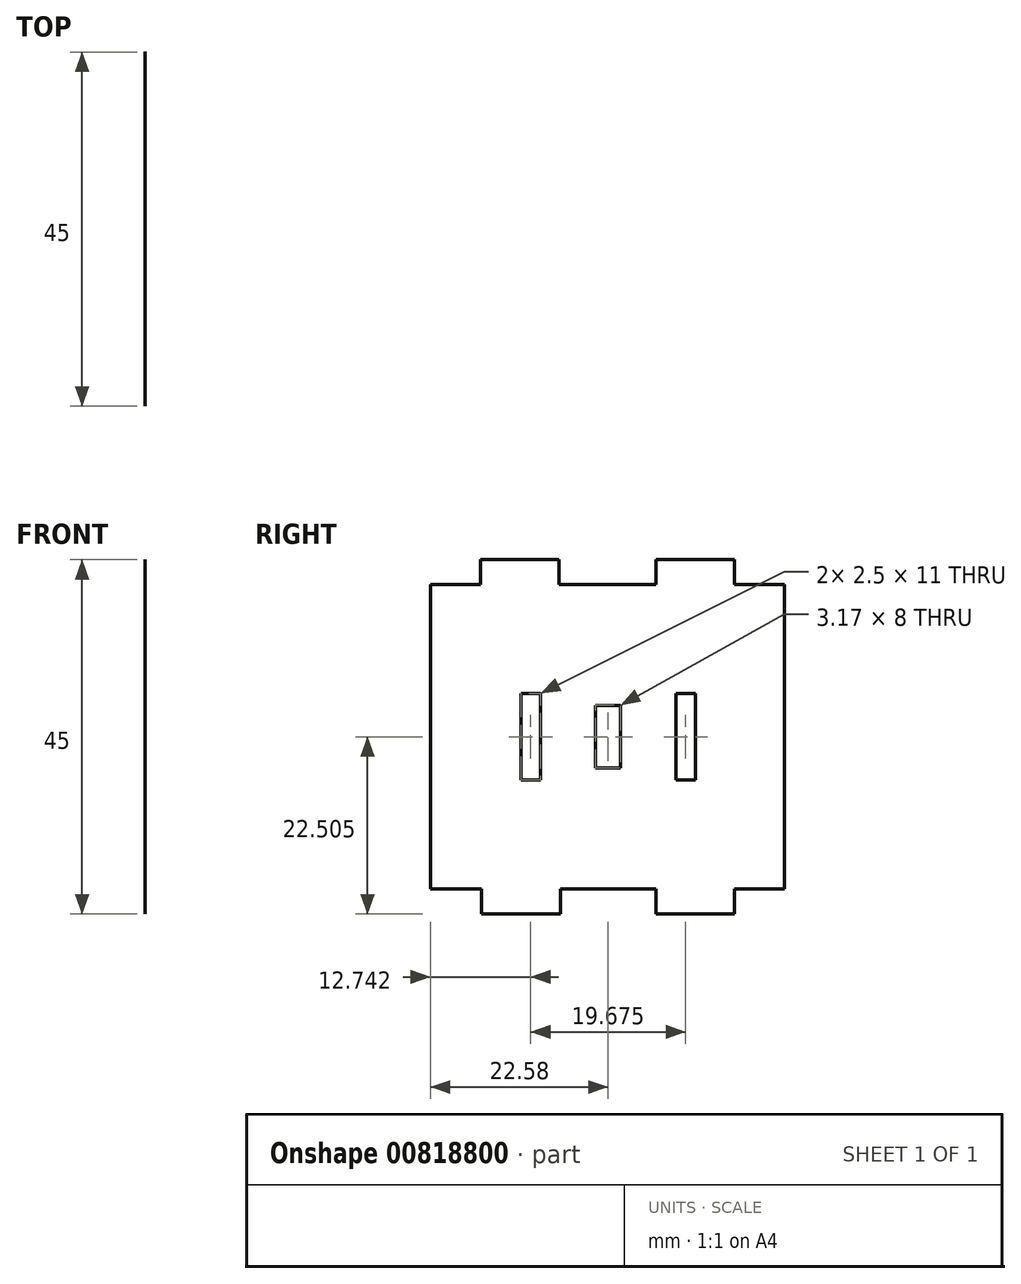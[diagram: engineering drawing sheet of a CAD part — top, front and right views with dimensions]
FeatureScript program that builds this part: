
annotation { "Feature Type Name" : "Feature", "Feature Type Description" : "" }
export const myFeature = defineFeature(function(context is Context, id is Id, definition is map)
    precondition{}
    {
        {
            var Q0;
            Q0=qCreatedBy(makeId("Right.planeOp"),FACE);
            var sketch = newSketch(context, id + "F0", { "sketchPlane" : qUnion([Q0])});
            skPoint(sketch, "E0.middle", {"position": v(0, 0) * mm});
            skLineSegment(sketch, "E1", {"start": v(16.07, -22.5) * mm, "end": v(16.07, -25.68) * mm});
            skLineSegment(sketch, "E2", {"start": v(16.07, -25.67) * mm, "end": v(6.07, -25.67) * mm});
            skLineSegment(sketch, "E3", {"start": v(6.07, -25.68) * mm, "end": v(6.07, -22.5) * mm});
            skLineSegment(sketch, "E4", {"start": v(6.07, -22.5) * mm, "end": v(-6.07, -22.5) * mm});
            skLineSegment(sketch, "E5", {"start": v(-6.07, -22.5) * mm, "end": v(-6.07, -25.68) * mm});
            skLineSegment(sketch, "E6", {"start": v(-6.07, -25.68) * mm, "end": v(-16.07, -25.68) * mm});
            skLineSegment(sketch, "E7", {"start": v(-16.07, -25.68) * mm, "end": v(-16.07, -22.5) * mm});
            skLineSegment(sketch, "E8", {"start": v(-16.07, -22.5) * mm, "end": v(-22.58, -22.5) * mm});
            skLineSegment(sketch, "E9", {"start": v(6.07, -24.09) * mm, "end": v(-6.07, -24.09) * mm});
            skPoint(sketch, "E10", {"position": v(0, -24.09) * mm});
            skLineSegment(sketch, "E11", {"start": v(16.07, 19.33) * mm, "end": v(6.07, 19.33) * mm});
            skLineSegment(sketch, "E12", {"start": v(6.07, 19.32) * mm, "end": v(6.07, 16.15) * mm});
            skLineSegment(sketch, "E13", {"start": v(6.07, 16.15) * mm, "end": v(-6.23, 16.15) * mm});
            skLineSegment(sketch, "E14", {"start": v(-6.23, 16.15) * mm, "end": v(-6.23, 19.33) * mm});
            skLineSegment(sketch, "E15", {"start": v(-6.23, 19.33) * mm, "end": v(-16.23, 19.33) * mm});
            skLineSegment(sketch, "E16", {"start": v(-16.23, 19.33) * mm, "end": v(-16.23, 16.15) * mm});
            skLineSegment(sketch, "E17", {"start": v(-16.23, 16.15) * mm, "end": v(-22.58, 16.15) * mm});
            skLineSegment(sketch, "E18", {"start": v(-22.58, 16.15) * mm, "end": v(-22.58, -22.5) * mm});
            skLineSegment(sketch, "E19", {"start": v(-19.4, 16.15) * mm, "end": v(-19.33, -22.5) * mm});
            skPoint(sketch, "E20", {"position": v(-19.36, -3.18) * mm});
            skLineSegment(sketch, "E21.bottom", {"start": v(1.59, -7.18) * mm, "end": v(-1.59, -7.18) * mm});
            skLineSegment(sketch, "E21.top", {"start": v(1.59, 0.82) * mm, "end": v(-1.59, 0.82) * mm});
            skLineSegment(sketch, "E21.left", {"start": v(1.59, -7.18) * mm, "end": v(1.59, 0.82) * mm});
            skLineSegment(sketch, "E21.right", {"start": v(-1.59, -7.18) * mm, "end": v(-1.59, 0.83) * mm});
            skPoint(sketch, "E21.middle", {"position": v(0, -3.18) * mm});
            skLineSegment(sketch, "E22.bottom", {"start": v(-8.59, 2.32) * mm, "end": v(-11.09, 2.32) * mm});
            skLineSegment(sketch, "E22.top", {"start": v(-8.59, -8.67) * mm, "end": v(-11.09, -8.67) * mm});
            skLineSegment(sketch, "E22.left", {"start": v(-8.59, 2.32) * mm, "end": v(-8.59, -8.67) * mm});
            skLineSegment(sketch, "E22.right", {"start": v(-11.09, 2.32) * mm, "end": v(-11.09, -8.67) * mm});
            skLineSegment(sketch, "E23", {"start": v(22.42, -22.5) * mm, "end": v(16.07, -22.5) * mm});
            skLineSegment(sketch, "E24", {"start": v(16.07, 19.32) * mm, "end": v(16.07, 16.15) * mm});
            skLineSegment(sketch, "E25", {"start": v(16.07, 16.15) * mm, "end": v(22.42, 16.15) * mm});
            skLineSegment(sketch, "E26", {"start": v(22.42, 16.15) * mm, "end": v(22.42, -22.5) * mm});
            skLineSegment(sketch, "E27.bottom", {"start": v(8.59, 2.33) * mm, "end": v(11.09, 2.33) * mm});
            skLineSegment(sketch, "E27.top", {"start": v(8.59, -8.67) * mm, "end": v(11.09, -8.67) * mm});
            skLineSegment(sketch, "E27.left", {"start": v(8.59, 2.32) * mm, "end": v(8.59, -8.67) * mm});
            skLineSegment(sketch, "E27.right", {"start": v(11.09, 2.32) * mm, "end": v(11.09, -8.67) * mm});
            skLineSegment(sketch, "E28", {"start": v(-1.59, -3.18) * mm, "end": v(-8.59, -3.18) * mm});
            skLineSegment(sketch, "E29", {"start": v(1.59, -3.18) * mm, "end": v(8.59, -3.17) * mm});
            skSolve(sketch);
        }
        {
            var Q0;
            Q0=makeQuery(id+"F0.imprint","IMPRINT",FACE,{"disambiguationData":[TD([[makeQuery(id+"F0.imprint","IMPRINT",EDGE,{"derivedFrom":sQuery(id+"F0.wireOp",EDGE,"E1")}),-1.0]])]});
            var Q1;
            {var subQ4=sQuery(id+"F0.wireOp",EDGE,"E18");Q1=makeQuery(id+"F0.imprint","IMPRINT",FACE,{"disambiguationData":[TD([[makeQuery(id+"F0.imprint","IMPRINT",EDGE,{"derivedFrom":subQ4}),1.0]])]});}
            extrude(context, id + "F1", {"entities" : qUnion([Q0, Q1]), "depth" : 1 / 203.2 * mm, "offsetDistance" : 25 * mm});
        }
    });
